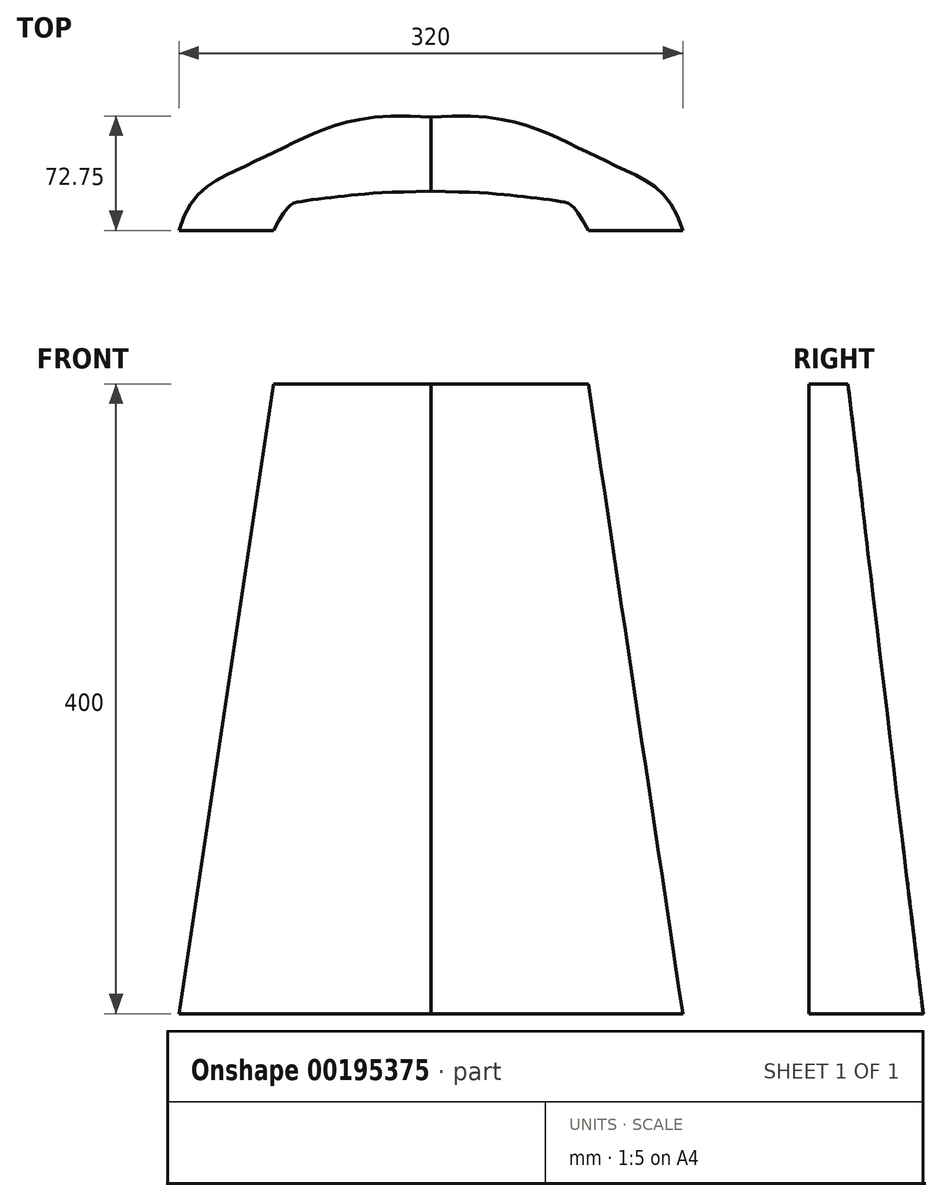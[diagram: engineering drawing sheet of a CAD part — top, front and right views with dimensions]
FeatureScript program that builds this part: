
annotation { "Feature Type Name" : "Feature", "Feature Type Description" : "" }
export const myFeature = defineFeature(function(context is Context, id is Id, definition is map)
    precondition{}
    {
        {
            var Q0;
            Q0=qCreatedBy(makeId("Top.planeOp"),FACE);
            var sketch = newSketch(context, id + "F0", { "sketchPlane" : qUnion([Q0])});
            skFitSpline(sketch, "E0", {"points": [v(-160, 0) * mm, v(-121.89, 38.97) * mm, v(-80.84, 58.6) * mm, v(0, 72.07) * mm], "startDerivative": vector(63.27, 235.33) * mm, "endDerivative": vector(326.8, -23.77) * mm});
            skSolve(sketch);
        }
        {
            var Q0;
            Q0=qCreatedBy(makeId("Top.planeOp"),FACE);
            cPlane(context, id + "F1", {"entities" : qUnion([Q0]), "cplaneType" : CPlaneType.OFFSET, "offset" : 400 * mm, "width" : 150 * mm, "height" : 150 * mm});
        }
        {
            var Q0;
            Q0=qCreatedBy(id+"F1.planeOp",FACE);
            var sketch = newSketch(context, id + "F2", { "sketchPlane" : qUnion([Q0])});
            skFitSpline(sketch, "E1", {"points": [v(-100, 0) * mm, v(-83.81, 18.1) * mm, v(-59.1, 21.48) * mm, v(0, 25) * mm], "startDerivative": vector(95.33, 173.1) * mm, "endDerivative": vector(227.85, 5.35) * mm});
            skSolve(sketch);
        }
        {
            var Q0;
            Q0=sQuery(id+"F0.wireOp",EDGE,"E0");
            var Q1;
            Q1=sQuery(id+"F2.wireOp",EDGE,"E1");
            loft(context, id + "F3", {"bodyType" : ToolBodyType.SURFACE, "wireProfilesArray" : [{ "wireProfileEntities" : qUnion([Q0]) }, { "wireProfileEntities" : qUnion([Q1]) }]});
        }
        {
            var Q0;
            Q0=makeQuery(id+"F3.opLoft","SWEPT_BODY",BODY,{"disambiguationData":[OSD([sQuery(id+"F0.wireOp",EDGE,"5083b6ae-aab3-4385-aa0b-1c0dbf534048"),sQuery(id+"F2.wireOp",EDGE,"E1")])]});
            var Q1;
            Q1=qCreatedBy(makeId("Right.planeOp"),FACE);
            mirror(context, id + "F4", {"entities" : qUnion([Q0]), "mirrorPlane" : qUnion([Q1])});
        }
    });
